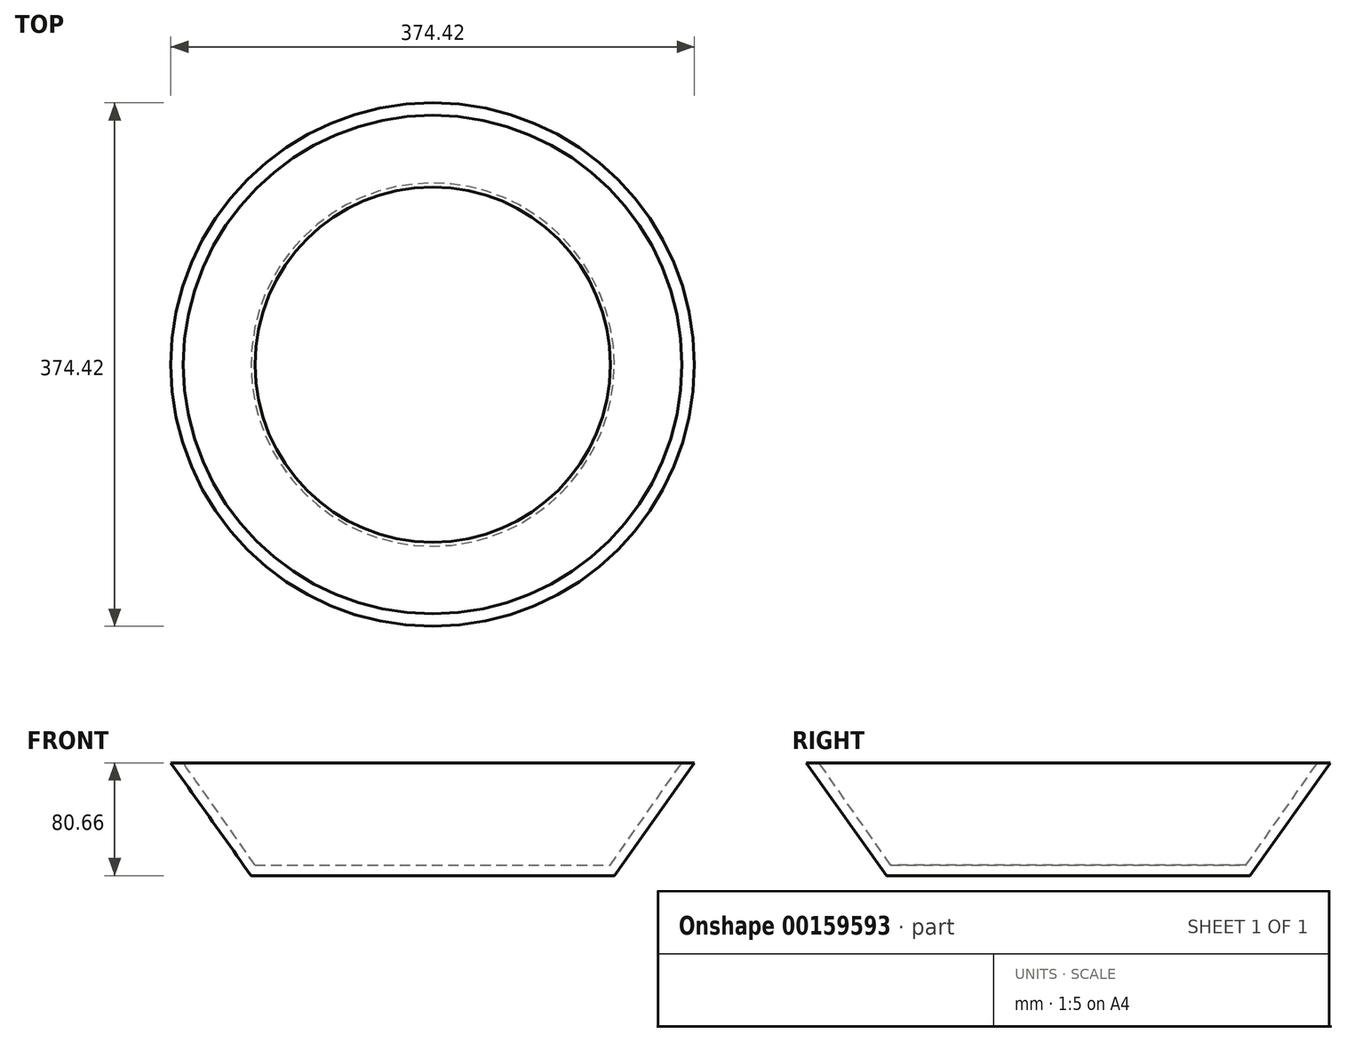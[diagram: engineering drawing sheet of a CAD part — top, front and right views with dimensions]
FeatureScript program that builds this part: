
annotation { "Feature Type Name" : "Feature", "Feature Type Description" : "" }
export const myFeature = defineFeature(function(context is Context, id is Id, definition is map)
    precondition{}
    {
        {
            var Q0;
            Q0=qCreatedBy(makeId("Front.planeOp"),FACE);
            var sketch = newSketch(context, id + "F0", { "sketchPlane" : qUnion([Q0])});
            skLineSegment(sketch, "E0", {"start": v(0, 0) * mm, "end": v(129.85, 0) * mm});
            skLineSegment(sketch, "E1", {"start": v(129.85, 0) * mm, "end": v(187.2, 80.66) * mm});
            skLineSegment(sketch, "E2", {"start": v(187.2, 80.66) * mm, "end": v(178.26, 80.66) * mm});
            skLineSegment(sketch, "E3", {"start": v(178.26, 80.66) * mm, "end": v(127, 7.43) * mm});
            skLineSegment(sketch, "E4", {"start": v(127, 7.43) * mm, "end": v(0, 7.43) * mm});
            skLineSegment(sketch, "E5", {"start": v(0, 7.43) * mm, "end": v(0, 0) * mm});
            skLineSegment(sketch, "E6", {"start": v(0, 0) * mm, "end": v(0, 127.6) * mm, "construction": true});
            skSolve(sketch);
        }
        {
            var Q0;
            Q0=makeQuery(id+"F0.imprint","IMPRINT",FACE,{"disambiguationData":[TD([[makeQuery(id+"F0.imprint","IMPRINT",EDGE,{"derivedFrom":sQuery(id+"F0.wireOp",EDGE,"E0")}),1.0]])]});
            var Q1;
            Q1=sQuery(id+"F0.wireOp",EDGE,"E6");
            revolve(context, id + "F1", {"entities" : qUnion([Q0]), "axis" : qUnion([Q1]), "revolveType" : RevolveType.FULL});
        }
    });
